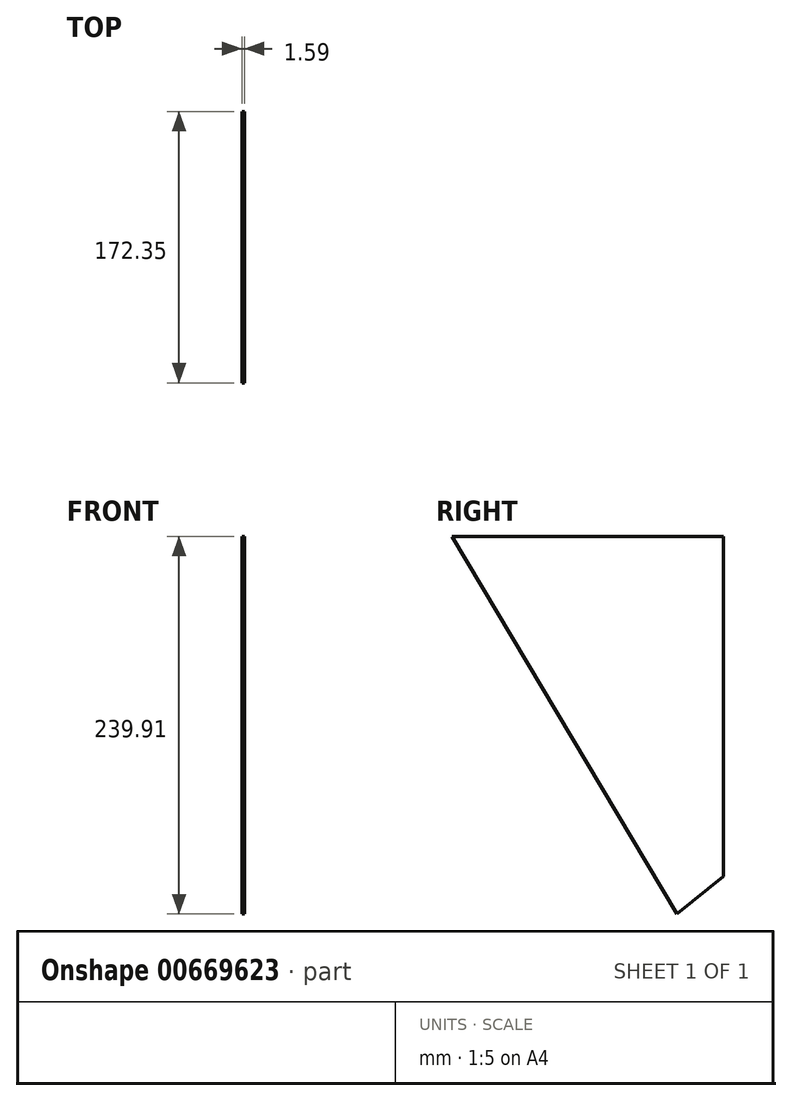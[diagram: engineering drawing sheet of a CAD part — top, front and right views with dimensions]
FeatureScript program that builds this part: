
annotation { "Feature Type Name" : "Feature", "Feature Type Description" : "" }
export const myFeature = defineFeature(function(context is Context, id is Id, definition is map)
    precondition{}
    {
        {
            var Q0;
            Q0=qCreatedBy(makeId("Right.planeOp"),FACE);
            var sketch = newSketch(context, id + "F0", { "sketchPlane" : qUnion([Q0])});
            skLineSegment(sketch, "E0", {"start": v(-98.12, 145.74) * mm, "end": v(74.23, 145.74) * mm});
            skLineSegment(sketch, "E1", {"start": v(74.23, 145.74) * mm, "end": v(74.23, -70.16) * mm});
            skLineSegment(sketch, "E2", {"start": v(74.23, -70.16) * mm, "end": v(44.64, -94.17) * mm});
            skLineSegment(sketch, "E3", {"start": v(44.64, -94.17) * mm, "end": v(-98.12, 145.74) * mm});
            skSolve(sketch);
        }
        {
            var Q0;
            Q0=qSketchRegion(id+"F0",true);
            extrude(context, id + "F1", {"entities" : qUnion([Q0]), "depth" : 1.59 * mm, "offsetDistance" : 25.4 * mm});
        }
    });
